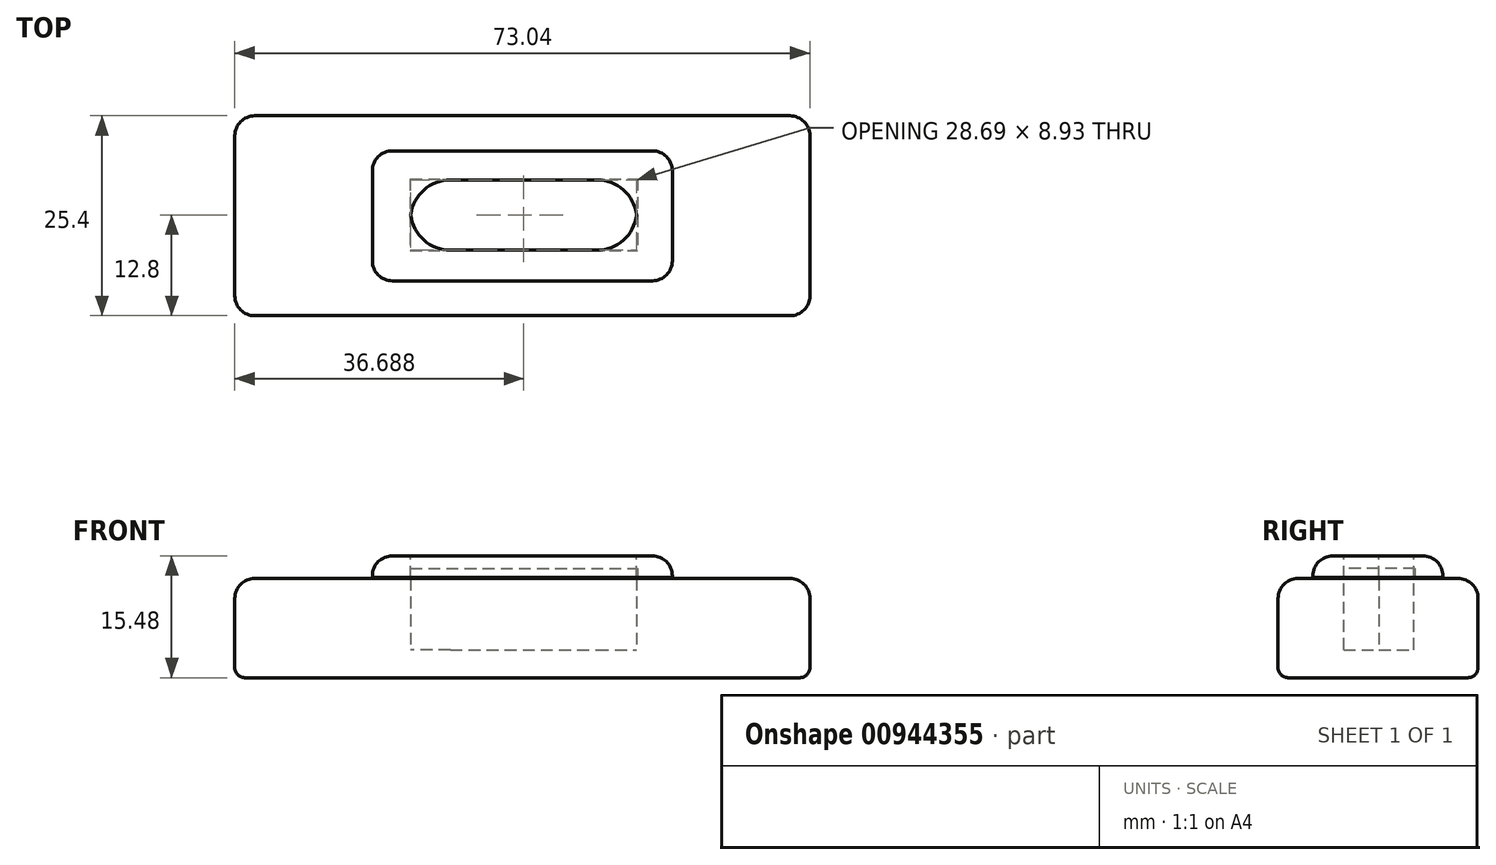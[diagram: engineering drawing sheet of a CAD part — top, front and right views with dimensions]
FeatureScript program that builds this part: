
annotation { "Feature Type Name" : "Feature", "Feature Type Description" : "" }
export const myFeature = defineFeature(function(context is Context, id is Id, definition is map)
    precondition{}
    {
        {
            var Q0;
            Q0=qCreatedBy(makeId("Front.planeOp"),FACE);
            var sketch = newSketch(context, id + "F0", { "sketchPlane" : qUnion([Q0])});
            skLineSegment(sketch, "E0.bottom", {"start": v(36.52, 6.3) * mm, "end": v(-36.52, 6.3) * mm});
            skLineSegment(sketch, "E0.top", {"start": v(36.52, -6.3) * mm, "end": v(-36.52, -6.3) * mm});
            skLineSegment(sketch, "E0.left", {"start": v(36.52, 6.3) * mm, "end": v(36.52, -6.3) * mm});
            skLineSegment(sketch, "E0.right", {"start": v(-36.52, 6.3) * mm, "end": v(-36.52, -6.3) * mm});
            skPoint(sketch, "E0.middle", {"position": v(0, 0) * mm});
            skSolve(sketch);
        }
        {
            var Q0;
            Q0=makeQuery(id+"F0.imprint","IMPRINT",FACE,{"disambiguationData":[TD([[makeQuery(id+"F0.imprint","IMPRINT",EDGE,{"derivedFrom":sQuery(id+"F0.wireOp",EDGE,"E0.bottom")}),1.0]])]});
            extrude(context, id + "F1", {"entities" : qUnion([Q0]), "endBound" : BoundingType.SYMMETRIC, "depth" : 25.4 * mm, "offsetDistance" : 25.4 * mm});
        }
        {
            var Q0;
            Q0=qCreatedBy(makeId("Right.planeOp"),FACE);
            var sketch = newSketch(context, id + "F2", { "sketchPlane" : qUnion([Q0])});
            skLineSegment(sketch, "E1.bottom", {"start": v(8.24, 6.4) * mm, "end": v(-8.26, 6.4) * mm});
            skLineSegment(sketch, "E1.top", {"start": v(8.24, 9.17) * mm, "end": v(-8.26, 9.17) * mm});
            skLineSegment(sketch, "E1.left", {"start": v(8.24, 6.4) * mm, "end": v(8.24, 9.17) * mm});
            skLineSegment(sketch, "E1.right", {"start": v(-8.26, 6.4) * mm, "end": v(-8.26, 9.17) * mm});
            skSolve(sketch);
        }
        {
            var Q0;
            Q0 = qSketchRegion(id + "F2", true);
            extrude(context, id + "F3", {"entities" : qUnion([Q0]), "endBound" : BoundingType.SYMMETRIC, "depth" : 38.1 * mm, "offsetDistance" : 25.4 * mm});
        }
        {
            var Q0;
            Q0=makeQuery(id+"F3.opExtrude","CAP_EDGE",EDGE,{"disambiguationData":[OSD([sQuery(id+"F2.wireOp",EDGE,"E1.right")])],"isStart":true});
            var Q1;
            Q1=makeQuery(id+"F3.opExtrude","CAP_EDGE",EDGE,{"disambiguationData":[OSD([sQuery(id+"F2.wireOp",EDGE,"E1.right")])],"isStart":false});
            var Q2;
            Q2=makeQuery(id+"F3.opExtrude","CAP_EDGE",EDGE,{"disambiguationData":[OSD([sQuery(id+"F2.wireOp",EDGE,"E1.left")])],"isStart":true});
            var Q3;
            Q3=makeQuery(id+"F3.opExtrude","CAP_EDGE",EDGE,{"disambiguationData":[OSD([sQuery(id+"F2.wireOp",EDGE,"E1.left")])],"isStart":false});
            var Q4;
            Q4=makeQuery(id+"F1.opExtrude","CAP_EDGE",EDGE,{"disambiguationData":[OSD([sQuery(id+"F0.wireOp",EDGE,"E0.right")])],"isStart":true});
            var Q5;
            Q5=makeQuery(id+"F1.opExtrude","CAP_EDGE",EDGE,{"disambiguationData":[OSD([sQuery(id+"F0.wireOp",EDGE,"E0.right")])],"isStart":false});
            var Q6;
            Q6=makeQuery(id+"F1.opExtrude","CAP_EDGE",EDGE,{"disambiguationData":[OSD([sQuery(id+"F0.wireOp",EDGE,"E0.left")])],"isStart":true});
            var Q7;
            Q7=makeQuery(id+"F1.opExtrude","CAP_EDGE",EDGE,{"disambiguationData":[OSD([sQuery(id+"F0.wireOp",EDGE,"E0.left")])],"isStart":false});
            fillet(context, id + "F4", {"entities" : qUnion([Q0, Q1, Q2, Q3, Q4, Q5, Q6, Q7]), "radius" : 2.54 * mm, "tangentPropagation" : true, "allowEdgeOverflow" : false});
        }
        {
            var Q0;
            Q0=makeQuery(id+"F4.opFillet","BLEND_EDGE",EDGE,{"blendedFrom":[makeQuery(id+"F1.opExtrude","CAP_EDGE",EDGE,{"disambiguationData":[OSD([sQuery(id+"F0.wireOp",EDGE,"E0.right")])],"isStart":true}),makeQuery(id+"F1.opExtrude","SWEPT_FACE",FACE,{"disambiguationData":[OSD([sQuery(id+"F0.wireOp",EDGE,"E0.bottom")])]})],"blendedInto":[makeQuery(id+"F1.opExtrude","SWEPT_FACE",FACE,{"disambiguationData":[OSD([sQuery(id+"F0.wireOp",EDGE,"E0.bottom")])]})]});
            fillet(context, id + "F5", {"entities" : qUnion([Q0]), "radius" : 2.54 * mm, "tangentPropagation" : true, "allowEdgeOverflow" : false});
        }
        {
            var Q0;
            Q0=makeQuery(id+"F3.opExtrude","SWEPT_FACE",FACE,{"disambiguationData":[OSD([sQuery(id+"F2.wireOp",EDGE,"E1.top")])]});
            var sketch = newSketch(context, id + "F6", { "sketchPlane" : qUnion([Q0])});
            skLineSegment(sketch, "E2.bottom", {"start": v(-14.21, 4.57) * mm, "end": v(14.55, 4.57) * mm});
            skLineSegment(sketch, "E2.top", {"start": v(-14.21, -4.37) * mm, "end": v(14.55, -4.37) * mm});
            skLineSegment(sketch, "E2.left", {"start": v(-14.21, 4.57) * mm, "end": v(-14.21, -4.37) * mm});
            skLineSegment(sketch, "E2.right", {"start": v(14.55, 4.57) * mm, "end": v(14.55, -4.37) * mm});
            skSolve(sketch);
        }
        {
            var Q0;
            Q0 = qSketchRegion(id + "F6", true);
            extrude(context, id + "F7", {"entities" : qUnion([Q0]), "operationType" : NewBodyOperationType.REMOVE, "depth" : 2.54 * mm, "offsetDistance" : 25.4 * mm});
        }
        {
            var Q0;
            Q0 = qSketchRegion(id + "F6", true);
            extrude(context, id + "F8", {"entities" : qUnion([Q0]), "operationType" : NewBodyOperationType.REMOVE, "oppositeDirection" : true, "depth" : 11.94 * mm, "offsetDistance" : 25.4 * mm});
        }
        {
            var Q0;
            Q0=makeQuery(id+"F8.boolean.opBoolean","COPY",EDGE,{"derivedFrom":makeQuery(id+"F8.opExtrude","SWEPT_EDGE",EDGE,{"disambiguationData":[OSD([sQuery(id+"F6.wireOp",EDGE,"E2.bottom"),sQuery(id+"F6.wireOp",EDGE,"E2.left")])]})});
            var Q1;
            Q1=makeQuery(id+"F8.boolean.opBoolean","COPY",EDGE,{"derivedFrom":makeQuery(id+"F8.opExtrude","SWEPT_EDGE",EDGE,{"disambiguationData":[OSD([sQuery(id+"F6.wireOp",EDGE,"E2.top"),sQuery(id+"F6.wireOp",EDGE,"E2.right")])]})});
            var Q2;
            Q2=makeQuery(id+"F8.boolean.opBoolean","COPY",EDGE,{"derivedFrom":makeQuery(id+"F8.opExtrude","SWEPT_EDGE",EDGE,{"disambiguationData":[OSD([sQuery(id+"F6.wireOp",EDGE,"E2.top"),sQuery(id+"F6.wireOp",EDGE,"E2.left")])]})});
            var Q3;
            Q3=makeQuery(id+"F8.boolean.opBoolean","COPY",EDGE,{"derivedFrom":makeQuery(id+"F8.opExtrude","SWEPT_EDGE",EDGE,{"disambiguationData":[OSD([sQuery(id+"F6.wireOp",EDGE,"E2.bottom"),sQuery(id+"F6.wireOp",EDGE,"E2.right")])]})});
            fillet(context, id + "F9", {"entities" : qUnion([Q0, Q1, Q2, Q3]), "radius" : 5.08 * mm, "tangentPropagation" : true, "allowEdgeOverflow" : false});
        }
        {
            var Q0;
            Q0=makeQuery(id+"F1.opExtrude","SWEPT_FACE",FACE,{"disambiguationData":[OSD([sQuery(id+"F0.wireOp",EDGE,"E0.bottom")])]});
            var sketch = newSketch(context, id + "F10", { "sketchPlane" : qUnion([Q0])});
            skLineSegment(sketch, "E3.bottom", {"start": v(-14.24, 4.7) * mm, "end": v(14.64, 4.7) * mm});
            skLineSegment(sketch, "E3.top", {"start": v(-14.24, -4.4) * mm, "end": v(14.64, -4.4) * mm});
            skLineSegment(sketch, "E3.left", {"start": v(-14.24, 4.7) * mm, "end": v(-14.24, -4.4) * mm});
            skLineSegment(sketch, "E3.right", {"start": v(14.64, 4.7) * mm, "end": v(14.64, -4.4) * mm});
            skSolve(sketch);
        }
        {
            var Q0;
            Q0 = qSketchRegion(id + "F10", true);
            extrude(context, id + "F11", {"entities" : qUnion([Q0]), "depth" : 1.27 * mm, "offsetDistance" : 25.4 * mm});
        }
        {
            var Q0;
            Q0=makeQuery(id+"F3.opExtrude","CAP_EDGE",EDGE,{"disambiguationData":[OSD([sQuery(id+"F2.wireOp",EDGE,"E1.top")])],"isStart":true});
            fillet(context, id + "F12", {"entities" : qUnion([Q0]), "radius" : 2.54 * mm, "tangentPropagation" : true, "allowEdgeOverflow" : false});
        }
        {
            var Q0;
            Q0=makeQuery(id+"F1.opExtrude","SWEPT_EDGE",EDGE,{"disambiguationData":[OSD([sQuery(id+"F0.wireOp",EDGE,"E0.top"),sQuery(id+"F0.wireOp",EDGE,"E0.right")])]});
            var Q1;
            Q1=makeQuery(id+"F1.opExtrude","CAP_EDGE",EDGE,{"disambiguationData":[OSD([sQuery(id+"F0.wireOp",EDGE,"E0.top")])],"isStart":false});
            var Q2;
            Q2=makeQuery(id+"F1.opExtrude","SWEPT_EDGE",EDGE,{"disambiguationData":[OSD([sQuery(id+"F0.wireOp",EDGE,"E0.top"),sQuery(id+"F0.wireOp",EDGE,"E0.left")])]});
            var Q3;
            Q3=makeQuery(id+"F1.opExtrude","CAP_EDGE",EDGE,{"disambiguationData":[OSD([sQuery(id+"F0.wireOp",EDGE,"E0.top")])],"isStart":true});
            var Q4;
            Q4=makeQuery(id+"F4.opFillet","BLEND_EDGE",EDGE,{"blendedFrom":[makeQuery(id+"F1.opExtrude","CAP_EDGE",EDGE,{"disambiguationData":[OSD([sQuery(id+"F0.wireOp",EDGE,"E0.right")])],"isStart":false}),makeQuery(id+"F1.opExtrude","SWEPT_FACE",FACE,{"disambiguationData":[OSD([sQuery(id+"F0.wireOp",EDGE,"E0.top")])]})],"blendedInto":[makeQuery(id+"F1.opExtrude","SWEPT_FACE",FACE,{"disambiguationData":[OSD([sQuery(id+"F0.wireOp",EDGE,"E0.top")])]})]});
            var Q5;
            Q5=makeQuery(id+"F4.opFillet","BLEND_EDGE",EDGE,{"blendedFrom":[makeQuery(id+"F1.opExtrude","CAP_EDGE",EDGE,{"disambiguationData":[OSD([sQuery(id+"F0.wireOp",EDGE,"E0.right")])],"isStart":true}),makeQuery(id+"F1.opExtrude","SWEPT_FACE",FACE,{"disambiguationData":[OSD([sQuery(id+"F0.wireOp",EDGE,"E0.top")])]})],"blendedInto":[makeQuery(id+"F1.opExtrude","SWEPT_FACE",FACE,{"disambiguationData":[OSD([sQuery(id+"F0.wireOp",EDGE,"E0.top")])]})]});
            var Q6;
            Q6=makeQuery(id+"F4.opFillet","BLEND_EDGE",EDGE,{"blendedFrom":[makeQuery(id+"F1.opExtrude","CAP_EDGE",EDGE,{"disambiguationData":[OSD([sQuery(id+"F0.wireOp",EDGE,"E0.left")])],"isStart":true}),makeQuery(id+"F1.opExtrude","SWEPT_FACE",FACE,{"disambiguationData":[OSD([sQuery(id+"F0.wireOp",EDGE,"E0.top")])]})],"blendedInto":[makeQuery(id+"F1.opExtrude","SWEPT_FACE",FACE,{"disambiguationData":[OSD([sQuery(id+"F0.wireOp",EDGE,"E0.top")])]})]});
            var Q7;
            Q7=makeQuery(id+"F4.opFillet","BLEND_EDGE",EDGE,{"blendedFrom":[makeQuery(id+"F1.opExtrude","CAP_EDGE",EDGE,{"disambiguationData":[OSD([sQuery(id+"F0.wireOp",EDGE,"E0.left")])],"isStart":false}),makeQuery(id+"F1.opExtrude","SWEPT_FACE",FACE,{"disambiguationData":[OSD([sQuery(id+"F0.wireOp",EDGE,"E0.top")])]})],"blendedInto":[makeQuery(id+"F1.opExtrude","SWEPT_FACE",FACE,{"disambiguationData":[OSD([sQuery(id+"F0.wireOp",EDGE,"E0.top")])]})]});
            fillet(context, id + "F13", {"entities" : qUnion([Q0, Q1, Q2, Q3, Q4, Q5, Q6, Q7]), "radius" : 1.27 * mm, "tangentPropagation" : true, "allowEdgeOverflow" : false});
        }
    });
